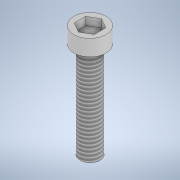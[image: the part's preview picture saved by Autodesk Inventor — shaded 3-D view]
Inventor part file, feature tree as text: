
AUTODESK INVENTOR PART (.ipt)
format: ipt  version: 2021 (Build 250183000, 183)  size: 124,416 bytes
history: native  units: mm
features: extrude x3, sketch x3, thread x1
ambient origin geometry x8: Origin, YZ Plane, XZ Plane, XY Plane, X Axis, Y Axis, Z Axis, Center Point
bodies: Solid1 (feature_tree)
feature tree (7):
  extrude  "Extrusion1"  Depth=2.0mm TaperAngle=0.0deg
  extrude  "Extrusion2"  Depth=12.0mm TaperAngle=0.0deg
  thread  "Thread1"  [1 undecoded]
  extrude  "Extrusion3"  [1 undecoded]
  sketch  "Sketch1"  dims[d0=4.0mm d1=2.0mm d2=0.0mm]
  sketch  "Sketch2"  dims[d3=2.5mm d4=12.0mm d5=0.0mm d6=12.0mm d7=0.0mm]
  sketch  "Sketch3"  dims[d8=1.0mm d9=0.0mm]
note: 2 required parameter values undecoded (feature->parameter linkage not recoverable at this tier; creation-order binding heuristic only, values carry confidence <= 0.55)
